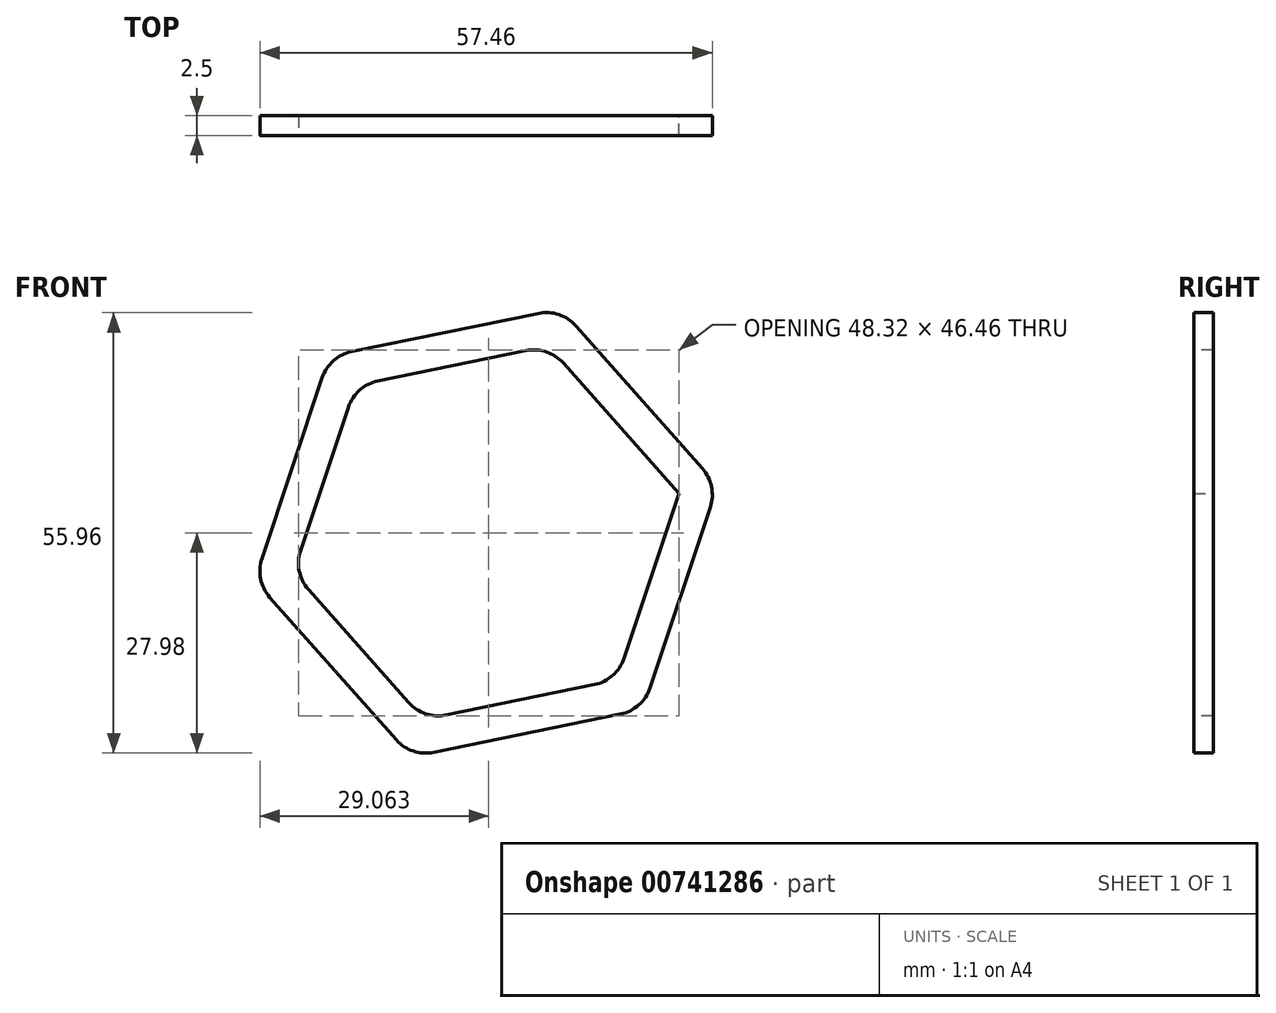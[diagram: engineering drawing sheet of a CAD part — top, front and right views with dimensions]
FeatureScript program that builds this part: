
annotation { "Feature Type Name" : "Feature", "Feature Type Description" : "" }
export const myFeature = defineFeature(function(context is Context, id is Id, definition is map)
    precondition{}
    {
        {
            var Q0;
            Q0=qCreatedBy(makeId("Front.planeOp"),FACE);
            var sketch = newSketch(context, id + "F0", { "sketchPlane" : qUnion([Q0])});
            skCircle(sketch, "E0.cCircle", {"center": v(0, 0) * mm, "radius": 30 * mm, "construction": true});
            skLineSegment(sketch, "E0.0", {"start": v(-19.9, 22.45) * mm, "end": v(9.49, 28.46) * mm});
            skLineSegment(sketch, "E0.1", {"start": v(9.49, 28.46) * mm, "end": v(29.4, 6.01) * mm});
            skLineSegment(sketch, "E0.2", {"start": v(29.4, 6.01) * mm, "end": v(19.9, -22.45) * mm});
            skLineSegment(sketch, "E0.3", {"start": v(19.9, -22.45) * mm, "end": v(-9.49, -28.46) * mm});
            skLineSegment(sketch, "E0.4", {"start": v(-9.49, -28.46) * mm, "end": v(-29.4, -6.01) * mm});
            skLineSegment(sketch, "E0.5", {"start": v(-29.4, -6.01) * mm, "end": v(-19.9, 22.45) * mm});
            skCircle(sketch, "E1.cCircle", {"center": v(0, 0) * mm, "radius": 25 * mm, "construction": true});
            skLineSegment(sketch, "E1.0", {"start": v(7.9, 23.72) * mm, "end": v(24.5, 5.01) * mm});
            skLineSegment(sketch, "E1.1", {"start": v(24.5, 5.01) * mm, "end": v(16.59, -18.7) * mm});
            skLineSegment(sketch, "E1.2", {"start": v(16.59, -18.7) * mm, "end": v(-7.9, -23.72) * mm});
            skLineSegment(sketch, "E1.3", {"start": v(-7.9, -23.72) * mm, "end": v(-24.5, -5.01) * mm});
            skLineSegment(sketch, "E1.4", {"start": v(-24.5, -5.01) * mm, "end": v(-16.59, 18.7) * mm});
            skLineSegment(sketch, "E1.5", {"start": v(-16.59, 18.7) * mm, "end": v(7.9, 23.72) * mm});
            skSolve(sketch);
        }
        {
            var Q0;
            Q0=makeQuery(id+"F0.imprint","IMPRINT",FACE,{"disambiguationData":[TD([[makeQuery(id+"F0.imprint","IMPRINT",EDGE,{"derivedFrom":sQuery(id+"F0.wireOp",EDGE,"E0.0")}),-1.0]])]});
            extrude(context, id + "F1", {"entities" : qUnion([Q0]), "depth" : 2.5 * mm, "offsetDistance" : 25 * mm});
        }
        {
            var Q0;
            Q0=makeQuery(id+"F1.opExtrude","SWEPT_EDGE",EDGE,{"disambiguationData":[OSD([sQuery(id+"F0.wireOp",EDGE,"E0.0"),sQuery(id+"F0.wireOp",EDGE,"E0.5")])]});
            var Q1;
            Q1=makeQuery(id+"F1.opExtrude","SWEPT_EDGE",EDGE,{"disambiguationData":[OSD([sQuery(id+"F0.wireOp",EDGE,"E0.0"),sQuery(id+"F0.wireOp",EDGE,"E0.1")])]});
            var Q2;
            Q2=makeQuery(id+"F1.opExtrude","SWEPT_EDGE",EDGE,{"disambiguationData":[OSD([sQuery(id+"F0.wireOp",EDGE,"E0.1"),sQuery(id+"F0.wireOp",EDGE,"E0.2")])]});
            var Q3;
            Q3=makeQuery(id+"F1.opExtrude","SWEPT_EDGE",EDGE,{"disambiguationData":[OSD([sQuery(id+"F0.wireOp",EDGE,"E0.2"),sQuery(id+"F0.wireOp",EDGE,"E0.3")])]});
            var Q4;
            Q4=makeQuery(id+"F1.opExtrude","SWEPT_EDGE",EDGE,{"disambiguationData":[OSD([sQuery(id+"F0.wireOp",EDGE,"E0.3"),sQuery(id+"F0.wireOp",EDGE,"E0.4")])]});
            var Q5;
            Q5=makeQuery(id+"F1.opExtrude","SWEPT_EDGE",EDGE,{"disambiguationData":[OSD([sQuery(id+"F0.wireOp",EDGE,"E0.4"),sQuery(id+"F0.wireOp",EDGE,"E0.5")])]});
            fillet(context, id + "F2", {"entities" : qUnion([Q0, Q1, Q2, Q3, Q4, Q5]), "radius" : 5 * mm, "tangentPropagation" : true, "allowEdgeOverflow" : false});
        }
        {
            var Q0;
            Q0=makeQuery(id+"F1.opExtrude","SWEPT_EDGE",EDGE,{"disambiguationData":[OSD([sQuery(id+"F0.wireOp",EDGE,"E1.3"),sQuery(id+"F0.wireOp",EDGE,"E1.4")])]});
            var Q1;
            Q1=makeQuery(id+"F1.opExtrude","SWEPT_EDGE",EDGE,{"disambiguationData":[OSD([sQuery(id+"F0.wireOp",EDGE,"E1.2"),sQuery(id+"F0.wireOp",EDGE,"E1.3")])]});
            var Q2;
            Q2=makeQuery(id+"F1.opExtrude","SWEPT_EDGE",EDGE,{"disambiguationData":[OSD([sQuery(id+"F0.wireOp",EDGE,"E1.1"),sQuery(id+"F0.wireOp",EDGE,"E1.2")])]});
            var Q3;
            Q3=makeQuery(id+"F1.opExtrude","SWEPT_EDGE",EDGE,{"disambiguationData":[OSD([sQuery(id+"F0.wireOp",EDGE,"E1.0"),sQuery(id+"F0.wireOp",EDGE,"E1.5")])]});
            var Q4;
            Q4=makeQuery(id+"F1.opExtrude","SWEPT_EDGE",EDGE,{"disambiguationData":[OSD([sQuery(id+"F0.wireOp",EDGE,"E1.4"),sQuery(id+"F0.wireOp",EDGE,"E1.5")])]});
            fillet(context, id + "F3", {"entities" : qUnion([Q0, Q1, Q2, Q3, Q4]), "radius" : 5 * mm, "tangentPropagation" : true, "allowEdgeOverflow" : false});
        }
    });
